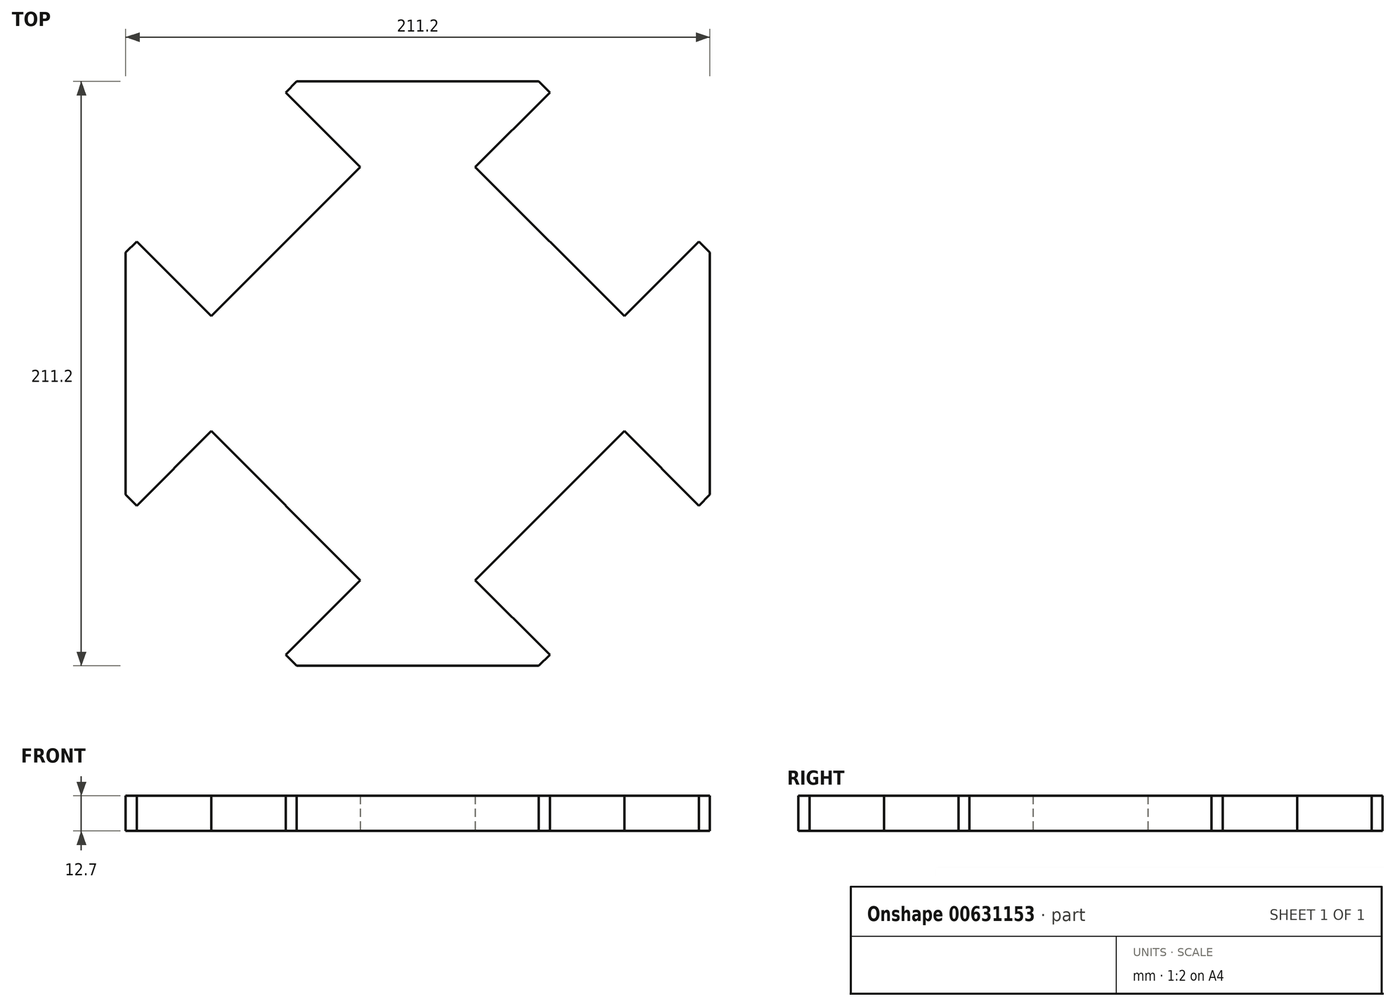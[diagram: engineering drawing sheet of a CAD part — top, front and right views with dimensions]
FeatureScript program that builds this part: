
annotation { "Feature Type Name" : "Feature", "Feature Type Description" : "" }
export const myFeature = defineFeature(function(context is Context, id is Id, definition is map)
    precondition{}
    {
        {
            var Q0;
            Q0=qCreatedBy(makeId("Top.planeOp"),FACE);
            var sketch = newSketch(context, id + "F0", { "sketchPlane" : qUnion([Q0])});
            skLineSegment(sketch, "E0", {"start": v(-52.54, 114.4) * mm, "end": v(34.94, 114.4) * mm});
            skLineSegment(sketch, "E1", {"start": v(34.94, 114.4) * mm, "end": v(96.8, 52.54) * mm});
            skLineSegment(sketch, "E2", {"start": v(96.8, 52.54) * mm, "end": v(96.8, -34.94) * mm});
            skLineSegment(sketch, "E3", {"start": v(96.8, -34.94) * mm, "end": v(34.94, -96.8) * mm});
            skLineSegment(sketch, "E4", {"start": v(34.94, -96.8) * mm, "end": v(-52.54, -96.8) * mm});
            skLineSegment(sketch, "E5", {"start": v(-52.54, -96.8) * mm, "end": v(-114.4, -34.94) * mm});
            skLineSegment(sketch, "E6", {"start": v(-114.4, -34.94) * mm, "end": v(-114.4, 52.54) * mm});
            skLineSegment(sketch, "E7", {"start": v(-114.4, 52.54) * mm, "end": v(-52.54, 114.4) * mm});
            skSolve(sketch);
        }
        {
            var Q0;
            Q0=makeQuery(id+"F0.imprint","IMPRINT",FACE,{"disambiguationData":[TD([[makeQuery(id+"F0.imprint","IMPRINT",EDGE,{"derivedFrom":sQuery(id+"F0.wireOp",EDGE,"E0")}),-1.0]])]});
            extrude(context, id + "F1", {"entities" : qUnion([Q0]), "depth" : 12.7 * mm, "offsetDistance" : 25.4 * mm});
        }
        {
            var Q0;
            Q0=makeQuery(id+"F1.opExtrude","SWEPT_FACE",FACE,{"disambiguationData":[OSD([sQuery(id+"F0.wireOp",EDGE,"E3")])]});
            var sketch = newSketch(context, id + "F2", { "sketchPlane" : qUnion([Q0])});
            skLineSegment(sketch, "E8.bottom", {"start": v(-38.1, 12.7) * mm, "end": v(38.1, 12.7) * mm});
            skLineSegment(sketch, "E8.top", {"start": v(-38.1, 0) * mm, "end": v(38.1, 0) * mm});
            skLineSegment(sketch, "E8.left", {"start": v(-38.1, 12.7) * mm, "end": v(-38.1, 0) * mm});
            skLineSegment(sketch, "E8.right", {"start": v(38.1, 12.7) * mm, "end": v(38.1, 0) * mm});
            skLineSegment(sketch, "E9", {"start": v(-38.1, 12.7) * mm, "end": v(-43.74, 12.7) * mm});
            skLineSegment(sketch, "E10", {"start": v(-43.74, 12.7) * mm, "end": v(-38.1, 12.7) * mm});
            skLineSegment(sketch, "E11", {"start": v(38.1, 12.7) * mm, "end": v(43.74, 12.7) * mm});
            skLineSegment(sketch, "E12", {"start": v(43.74, 12.7) * mm, "end": v(38.1, 12.7) * mm});
            skSolve(sketch);
        }
        {
            var Q0;
            Q0=makeQuery(id+"F2.imprint","IMPRINT",FACE,{"disambiguationData":[TD([[makeQuery(id+"F2.imprint","IMPRINT",EDGE,{"derivedFrom":sQuery(id+"F2.wireOp",EDGE,"E8.bottom")}),1.0]])]});
            extrude(context, id + "F3", {"entities" : qUnion([Q0]), "operationType" : NewBodyOperationType.REMOVE, "oppositeDirection" : true, "depth" : 38.1 * mm, "offsetDistance" : 25.4 * mm});
        }
        {
            var Q0;
            Q0=makeQuery(id+"F1.opExtrude","SWEPT_FACE",FACE,{"disambiguationData":[OSD([sQuery(id+"F0.wireOp",EDGE,"E5")])]});
            var sketch = newSketch(context, id + "F4", { "sketchPlane" : qUnion([Q0])});
            skLineSegment(sketch, "E13.bottom", {"start": v(-50.55, 12.7) * mm, "end": v(25.65, 12.7) * mm});
            skLineSegment(sketch, "E13.top", {"start": v(-50.55, 0) * mm, "end": v(25.65, 0) * mm});
            skLineSegment(sketch, "E13.left", {"start": v(-50.55, 12.7) * mm, "end": v(-50.55, 0) * mm});
            skLineSegment(sketch, "E13.right", {"start": v(25.65, 12.7) * mm, "end": v(25.65, 0) * mm});
            skLineSegment(sketch, "E14", {"start": v(-56.19, 12.7) * mm, "end": v(-50.55, 12.7) * mm});
            skLineSegment(sketch, "E15", {"start": v(25.65, 12.7) * mm, "end": v(31.3, 12.7) * mm});
            skSolve(sketch);
        }
        {
            var Q0;
            Q0=makeQuery(id+"F4.imprint","IMPRINT",FACE,{"disambiguationData":[TD([[makeQuery(id+"F4.imprint","IMPRINT",EDGE,{"derivedFrom":sQuery(id+"F4.wireOp",EDGE,"E13.bottom")}),1.0]])]});
            extrude(context, id + "F5", {"entities" : qUnion([Q0]), "operationType" : NewBodyOperationType.REMOVE, "oppositeDirection" : true, "depth" : 38.1 * mm, "offsetDistance" : 25.4 * mm});
        }
        {
            var Q0;
            Q0=makeQuery(id+"F1.opExtrude","SWEPT_FACE",FACE,{"disambiguationData":[OSD([sQuery(id+"F0.wireOp",EDGE,"E7")])]});
            var sketch = newSketch(context, id + "F6", { "sketchPlane" : qUnion([Q0])});
            skLineSegment(sketch, "E16.bottom", {"start": v(-38.1, 12.7) * mm, "end": v(38.1, 12.7) * mm});
            skLineSegment(sketch, "E16.top", {"start": v(-38.1, 0) * mm, "end": v(38.1, 0) * mm});
            skLineSegment(sketch, "E16.left", {"start": v(-38.1, 12.7) * mm, "end": v(-38.1, 0) * mm});
            skLineSegment(sketch, "E16.right", {"start": v(38.1, 12.7) * mm, "end": v(38.1, 0) * mm});
            skLineSegment(sketch, "E17", {"start": v(-43.74, 12.7) * mm, "end": v(-38.1, 12.7) * mm});
            skLineSegment(sketch, "E18", {"start": v(38.1, 12.7) * mm, "end": v(43.74, 12.7) * mm});
            skSolve(sketch);
        }
        {
            var Q0;
            Q0=makeQuery(id+"F6.imprint","IMPRINT",FACE,{"disambiguationData":[TD([[makeQuery(id+"F6.imprint","IMPRINT",EDGE,{"derivedFrom":sQuery(id+"F6.wireOp",EDGE,"E16.bottom")}),1.0]])]});
            extrude(context, id + "F7", {"entities" : qUnion([Q0]), "operationType" : NewBodyOperationType.REMOVE, "oppositeDirection" : true, "depth" : 38.1 * mm, "offsetDistance" : 25.4 * mm});
        }
        {
            var Q0;
            Q0=makeQuery(id+"F1.opExtrude","SWEPT_FACE",FACE,{"disambiguationData":[OSD([sQuery(id+"F0.wireOp",EDGE,"E1")])]});
            var sketch = newSketch(context, id + "F8", { "sketchPlane" : qUnion([Q0])});
            skLineSegment(sketch, "E19.bottom", {"start": v(-25.65, 12.7) * mm, "end": v(50.55, 12.7) * mm});
            skLineSegment(sketch, "E19.top", {"start": v(-25.65, 0) * mm, "end": v(50.55, 0) * mm});
            skLineSegment(sketch, "E19.left", {"start": v(-25.65, 12.7) * mm, "end": v(-25.65, 0) * mm});
            skLineSegment(sketch, "E19.right", {"start": v(50.55, 12.7) * mm, "end": v(50.55, 0) * mm});
            skLineSegment(sketch, "E20", {"start": v(-31.3, 12.7) * mm, "end": v(-25.65, 12.7) * mm});
            skLineSegment(sketch, "E21", {"start": v(50.55, 12.7) * mm, "end": v(56.19, 12.7) * mm});
            skSolve(sketch);
        }
        {
            var Q0;
            Q0=makeQuery(id+"F8.imprint","IMPRINT",FACE,{"disambiguationData":[TD([[makeQuery(id+"F8.imprint","IMPRINT",EDGE,{"derivedFrom":sQuery(id+"F8.wireOp",EDGE,"E19.bottom")}),1.0]])]});
            extrude(context, id + "F9", {"entities" : qUnion([Q0]), "operationType" : NewBodyOperationType.REMOVE, "oppositeDirection" : true, "depth" : 38.1 * mm, "offsetDistance" : 25.4 * mm});
        }
    });
